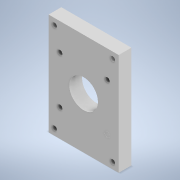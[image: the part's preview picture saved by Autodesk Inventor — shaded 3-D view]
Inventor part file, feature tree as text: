
AUTODESK INVENTOR PART (.ipt)
format: ipt  version: 2020 (Build 240168000, 168)  size: 128,000 bytes
history: native  units: in
note: dims shown in document units (in); Inventor stores cm internally (conversion verified against a paired STEP export)
features: reference x7, other x6, extrude x3, sketch x3
ambient origin geometry x8: Origin, YZ Plane, XZ Plane, XY Plane, X Axis, Y Axis, Z Axis, Center Point
bodies: Solid1 (feature_tree)
feature tree (19):
  extrude  "Extrusion1"  Depth=0.5in TaperAngle=0.0deg
  extrude  "Extrusion2"  Depth=0.1875in
  extrude  "Extrusion3"  Depth=0.1875in
  sketch  "Sketch1"  dims[d0=0.5in d1=0.0in d2=0.5in d3=0.0in]
  reference  "Reference1"
  reference  "Reference2"
  sketch  "Sketch2"  dims[d4=0.1875in d5=0.1875in]
  reference  "Reference3"
  sketch  "Sketch3"  dims[d6=0.1875in d7=0.1875in d8=1.0in d9=0.0in]
  reference  "Reference4"
  reference  "Reference5"
  reference  "Reference6"
  reference  "Reference7"
  other  "<userpath>\Desktop\PnP Machine\PnP Machine.iam"
  other  "PnP Machine.iam"
  other  "Stepper Standoff:4"
  other  "Stepper Standoff:3"
  other  "6384K361_BALL BEARING:1"
  other  "ST5918L4508-A:1"
